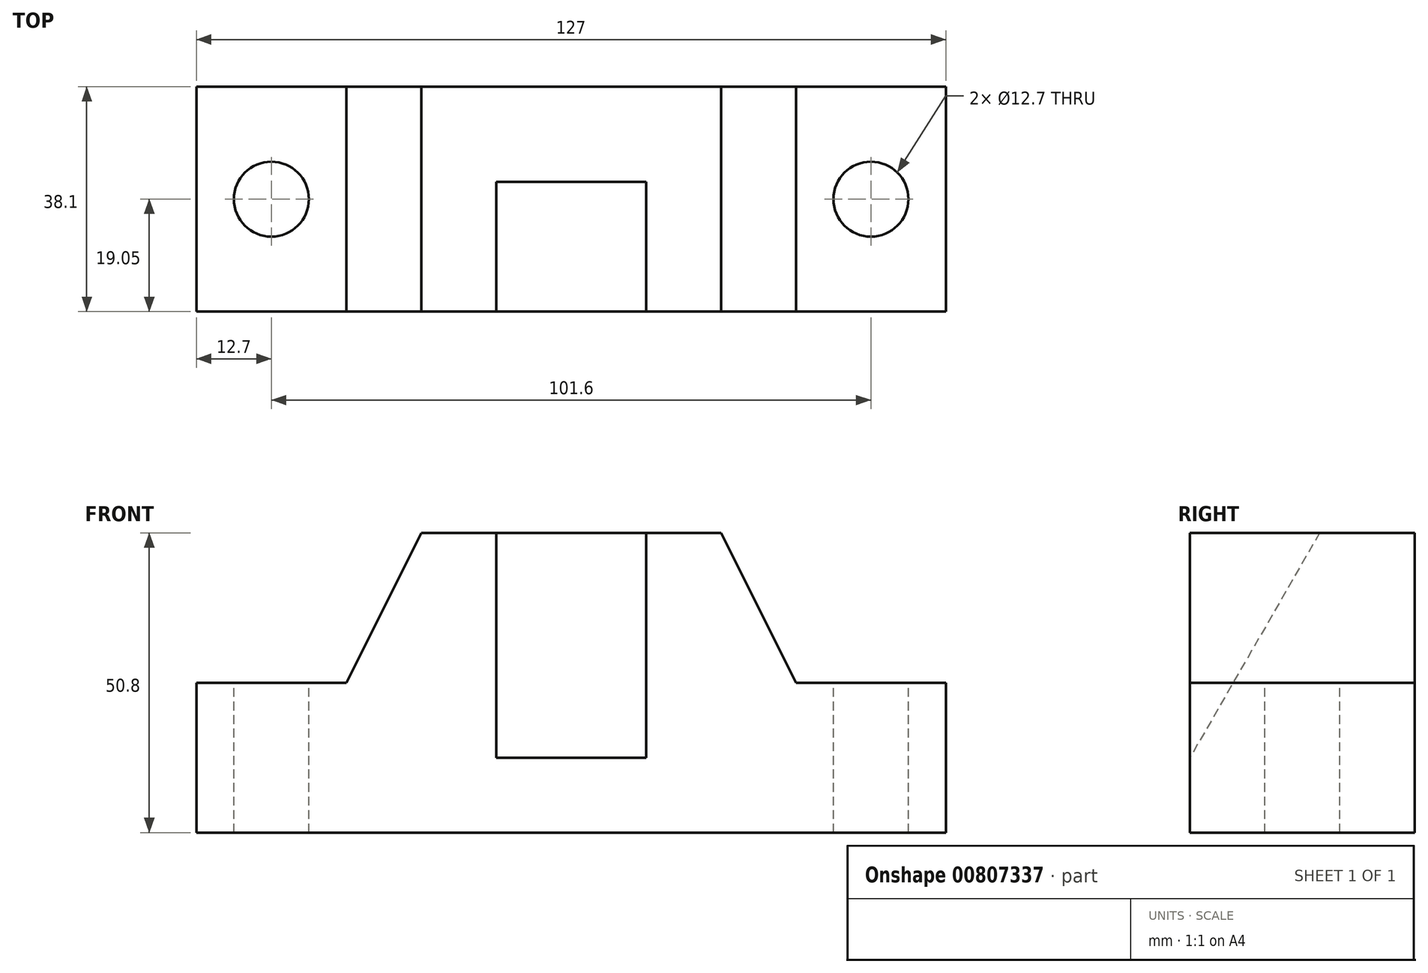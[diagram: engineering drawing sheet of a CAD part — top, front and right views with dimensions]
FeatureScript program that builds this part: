
annotation { "Feature Type Name" : "Feature", "Feature Type Description" : "" }
export const myFeature = defineFeature(function(context is Context, id is Id, definition is map)
    precondition{}
    {
        {
            var Q0;
            Q0=qCreatedBy(makeId("Front.planeOp"),FACE);
            var sketch = newSketch(context, id + "F0", { "sketchPlane" : qUnion([Q0])});
            skLineSegment(sketch, "E0", {"start": v(0, 0) * mm, "end": v(127, 0) * mm});
            skLineSegment(sketch, "E1", {"start": v(127, 0) * mm, "end": v(127, 25.4) * mm});
            skLineSegment(sketch, "E2", {"start": v(127, 25.4) * mm, "end": v(101.6, 25.4) * mm});
            skLineSegment(sketch, "E3", {"start": v(101.6, 25.4) * mm, "end": v(88.9, 50.8) * mm});
            skLineSegment(sketch, "E4", {"start": v(88.9, 50.8) * mm, "end": v(38.1, 50.8) * mm});
            skLineSegment(sketch, "E5", {"start": v(38.1, 50.8) * mm, "end": v(25.4, 25.4) * mm});
            skLineSegment(sketch, "E6", {"start": v(25.4, 25.4) * mm, "end": v(0, 25.4) * mm});
            skLineSegment(sketch, "E7", {"start": v(0, 25.4) * mm, "end": v(0, 0) * mm});
            skPoint(sketch, "E8", {"position": v(12.7, 25.4) * mm});
            skPoint(sketch, "E9", {"position": v(114.3, 25.4) * mm});
            skSolve(sketch);
        }
        {
            var Q0;
            Q0=makeQuery(id+"F0.imprint","IMPRINT",FACE,{"disambiguationData":[TD([[makeQuery(id+"F0.imprint","IMPRINT",EDGE,{"derivedFrom":sQuery(id+"F0.wireOp",EDGE,"E0")}),1.0]])]});
            extrude(context, id + "F1", {"entities" : qUnion([Q0]), "endBound" : BoundingType.SYMMETRIC, "oppositeDirection" : true, "depth" : 38.1 * mm, "offsetDistance" : 25.4 * mm});
        }
        {
            var Q0;
            Q0=makeQuery(id+"F1.opExtrude","SWEPT_FACE",FACE,{"disambiguationData":[OSD([sQuery(id+"F0.wireOp",EDGE,"E6")])]});
            var sketch = newSketch(context, id + "F2", { "sketchPlane" : qUnion([Q0])});
            skPoint(sketch, "E10.0", {"position": v(12.7, 0) * mm});
            skPoint(sketch, "E11.0", {"position": v(114.3, 0) * mm});
            skSolve(sketch);
        }
        {
            var Q0;
            Q0=sQuery(id+"F2.wireOp",VERTEX,"E10.0");
            var Q1;
            Q1=sQuery(id+"F2.wireOp",VERTEX,"E11.0");
            var Q2;
            Q2=makeQuery(id+"F1.opExtrude","SWEPT_BODY",BODY,{"disambiguationData":[OSD([sQuery(id+"F0.wireOp",EDGE,"E0"),sQuery(id+"F0.wireOp",EDGE,"E1"),sQuery(id+"F0.wireOp",EDGE,"E2"),sQuery(id+"F0.wireOp",EDGE,"E3"),sQuery(id+"F0.wireOp",EDGE,"E4"),sQuery(id+"F0.wireOp",EDGE,"E5"),sQuery(id+"F0.wireOp",EDGE,"E6"),sQuery(id+"F0.wireOp",EDGE,"E7")])]});
            hole(context, id + "F3", {"style" : HoleStyle.SIMPLE, "endStyle" : HoleEndStyle.BLIND, "holeDiameter" : 12.7 * mm, "majorDiameter" : 6.35 * mm, "holeDepth" : 31.75 * mm, "isTappedThrough" : true, "tappedDepth" : 12.7 * mm, "tapClearance" : 3, "startFromSketch" : true, "locations" : qUnion([Q0, Q1]), "scope" : qUnion([Q2])});
        }
        {
            var Q0;
            Q0=qCreatedBy(makeId("Right.planeOp"),FACE);
            cPlane(context, id + "F4", {"entities" : qUnion([Q0]), "cplaneType" : CPlaneType.OFFSET, "offset" : 63.5 * mm, "width" : 152.4 * mm, "height" : 152.4 * mm});
        }
        {
            var Q0;
            Q0=qCreatedBy(id+"F4.planeOp",FACE);
            var sketch = newSketch(context, id + "F5", { "sketchPlane" : qUnion([Q0])});
            skLineSegment(sketch, "E12.0", {"start": v(19.05, 50.8) * mm, "end": v(-19.05, 50.8) * mm});
            skPoint(sketch, "E13.0", {"position": v(0, 50.8) * mm});
            skLineSegment(sketch, "E14.0", {"start": v(19.05, 0) * mm, "end": v(-19.05, 0) * mm});
            skLineSegment(sketch, "E15", {"start": v(-19.05, 50.8) * mm, "end": v(-19.05, 0) * mm});
            skLineSegment(sketch, "E16", {"start": v(2.95, 50.8) * mm, "end": v(-19.05, 12.7) * mm});
            skSolve(sketch);
        }
        {
            var Q0;
            {var subQ3=sQuery(id+"F5.wireOp",EDGE,"E16");Q0=makeQuery(id+"F5.imprint","IMPRINT",FACE,{"disambiguationData":[TD([[makeQuery(id+"F5.imprint","IMPRINT",EDGE,{"derivedFrom":subQ3}),-1.0]])]});}
            extrude(context, id + "F6", {"entities" : qUnion([Q0]), "operationType" : NewBodyOperationType.REMOVE, "endBound" : BoundingType.SYMMETRIC, "oppositeDirection" : true, "depth" : 25.4 * mm, "offsetDistance" : 25.4 * mm});
        }
    });
